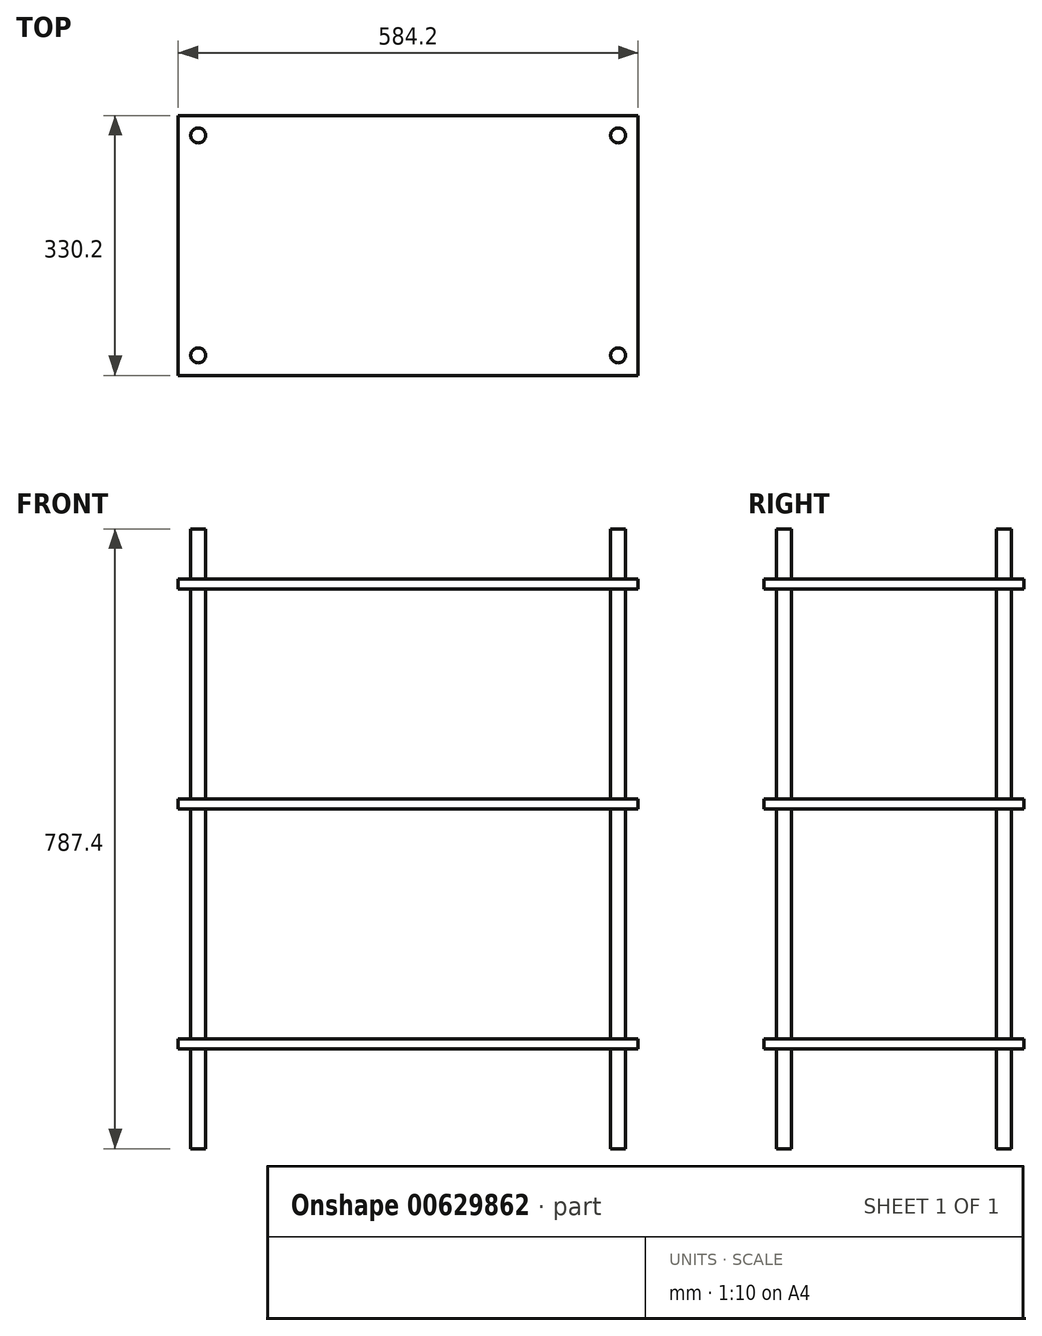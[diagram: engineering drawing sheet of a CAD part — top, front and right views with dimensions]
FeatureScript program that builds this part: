
annotation { "Feature Type Name" : "Feature", "Feature Type Description" : "" }
export const myFeature = defineFeature(function(context is Context, id is Id, definition is map)
    precondition{}
    {
        {
            var Q0;
            Q0=qCreatedBy(makeId("Top.planeOp"),FACE);
            var sketch = newSketch(context, id + "F0", { "sketchPlane" : qUnion([Q0])});
            skLineSegment(sketch, "E0.bottom", {"start": v(292.1, 165.1) * mm, "end": v(-292.1, 165.1) * mm});
            skLineSegment(sketch, "E0.top", {"start": v(292.1, -165.1) * mm, "end": v(-292.1, -165.1) * mm});
            skLineSegment(sketch, "E0.left", {"start": v(292.1, 165.1) * mm, "end": v(292.1, -165.1) * mm});
            skLineSegment(sketch, "E0.right", {"start": v(-292.1, 165.1) * mm, "end": v(-292.1, -165.1) * mm});
            skPoint(sketch, "E0.middle", {"position": v(0, 0) * mm});
            skCircle(sketch, "E1", {"center": v(-266.7, 139.7) * mm, "radius": 9.53 * mm});
            skSolve(sketch);
        }
        {
            var Q0;
            Q0=makeQuery(id+"F0.imprint","IMPRINT",FACE,{"disambiguationData":[TD([[makeQuery(id+"F0.imprint","IMPRINT",EDGE,{"derivedFrom":sQuery(id+"F0.wireOp",EDGE,"E1")}),1.0]])]});
            var Q1;
            Q1=sQuery(id+"F0.wireOp",EDGE,"E1");
            extrude(context, id + "F1", {"entities" : qUnion([Q0]), "surfaceEntities" : qUnion([Q1]), "depth" : 787.4 * mm, "offsetDistance" : 25.4 * mm});
        }
        {
            var Q0;
            Q0=makeQuery(id+"F1.opExtrude","SWEPT_BODY",BODY,{"disambiguationData":[OSD([sQuery(id+"F0.wireOp",EDGE,"E1")])]});
            var Q1;
            Q1=qCreatedBy(makeId("Front.planeOp"),FACE);
            mirror(context, id + "F2", {"entities" : qUnion([Q0]), "mirrorPlane" : qUnion([Q1])});
        }
        {
            var Q0;
            Q0=makeQuery(id+"F1.opExtrude","SWEPT_BODY",BODY,{"disambiguationData":[OSD([sQuery(id+"F0.wireOp",EDGE,"E1")])]});
            var Q1;
            Q1=makeQuery(id+"F2.opPattern","COPY",BODY,{"derivedFrom":makeQuery(id+"F1.opExtrude","SWEPT_BODY",BODY,{"disambiguationData":[OSD([sQuery(id+"F0.wireOp",EDGE,"E1")])]}),"instanceName":"1"});
            var Q2;
            Q2=qCreatedBy(makeId("Right.planeOp"),FACE);
            mirror(context, id + "F3", {"entities" : qUnion([Q0, Q1]), "mirrorPlane" : qUnion([Q2])});
        }
        {
            var Q0;
            Q0=makeQuery(id+"F0.imprint","IMPRINT",FACE,{"disambiguationData":[TD([[makeQuery(id+"F0.imprint","IMPRINT",EDGE,{"derivedFrom":sQuery(id+"F0.wireOp",EDGE,"E0.bottom")}),1.0]])]});
            extrude(context, id + "F4", {"entities" : qUnion([Q0]), "operationType" : NewBodyOperationType.ADD, "depth" : 139.7 * mm, "offsetDistance" : 25.4 * mm, "hasSecondDirection" : true, "secondDirectionOppositeDirection" : false, "secondDirectionDepth" : 127 * mm});
        }
        {
            var Q0;
            Q0=makeQuery(id+"F0.imprint","IMPRINT",FACE,{"disambiguationData":[TD([[makeQuery(id+"F0.imprint","IMPRINT",EDGE,{"derivedFrom":sQuery(id+"F0.wireOp",EDGE,"E0.bottom")}),1.0]])]});
            extrude(context, id + "F5", {"entities" : qUnion([Q0]), "operationType" : NewBodyOperationType.ADD, "depth" : 444.5 * mm, "offsetDistance" : 25.4 * mm, "hasSecondDirection" : true, "secondDirectionOppositeDirection" : false, "secondDirectionDepth" : 431.8 * mm});
        }
        {
            var Q0;
            Q0=makeQuery(id+"F0.imprint","IMPRINT",FACE,{"disambiguationData":[TD([[makeQuery(id+"F0.imprint","IMPRINT",EDGE,{"derivedFrom":sQuery(id+"F0.wireOp",EDGE,"E0.bottom")}),1.0]])]});
            extrude(context, id + "F6", {"entities" : qUnion([Q0]), "operationType" : NewBodyOperationType.ADD, "depth" : 723.9 * mm, "offsetDistance" : 25.4 * mm, "hasSecondDirection" : true, "secondDirectionOppositeDirection" : false, "secondDirectionDepth" : 711.2 * mm});
        }
    });
